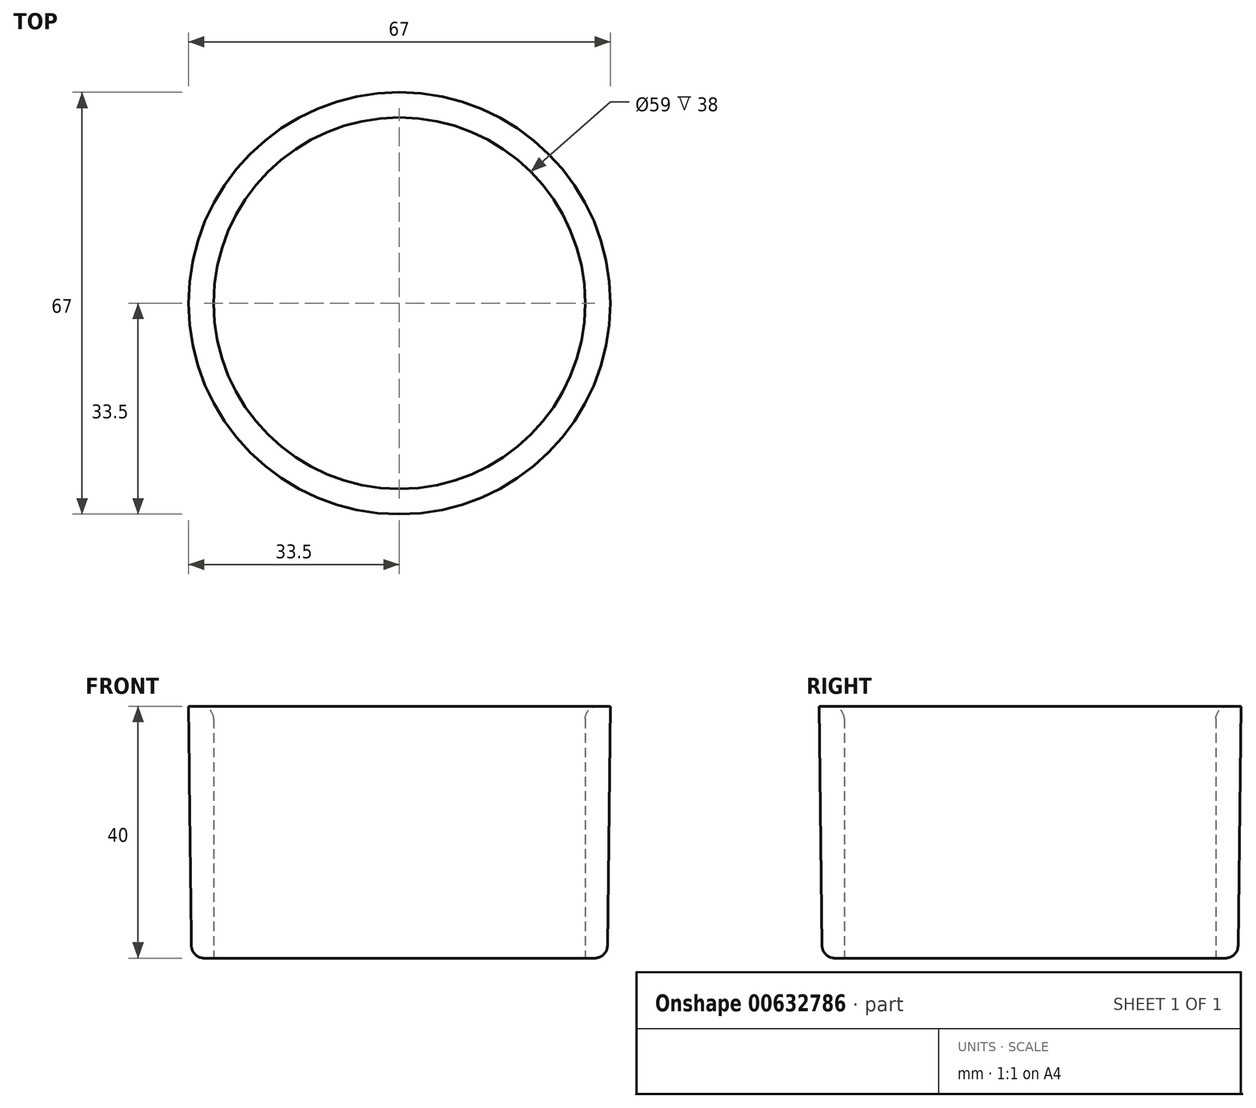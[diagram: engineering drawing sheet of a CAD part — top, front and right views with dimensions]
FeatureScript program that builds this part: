
annotation { "Feature Type Name" : "Feature", "Feature Type Description" : "" }
export const myFeature = defineFeature(function(context is Context, id is Id, definition is map)
    precondition{}
    {
        {
            var Q0;
            Q0=qCreatedBy(makeId("Front.planeOp"),FACE);
            var sketch = newSketch(context, id + "F0", { "sketchPlane" : qUnion([Q0])});
            skLineSegment(sketch, "E0", {"start": v(29.5, 0) * mm, "end": v(29.5, 40) * mm});
            skLineSegment(sketch, "E1", {"start": v(29.5, 40) * mm, "end": v(33.5, 40) * mm});
            skLineSegment(sketch, "E2", {"start": v(29.5, 0) * mm, "end": v(33.5, 0) * mm});
            skLineSegment(sketch, "E3", {"start": v(33.5, 40) * mm, "end": v(33.5, 0) * mm});
            skSolve(sketch);
        }
        {
            var Q0;
            Q0=qCreatedBy(makeId("Front.planeOp"),FACE);
            var sketch = newSketch(context, id + "F1", { "sketchPlane" : qUnion([Q0])});
            skLineSegment(sketch, "E4", {"start": v(0, 0) * mm, "end": v(0, 29.93) * mm});
            skSolve(sketch);
        }
        {
            var Q0;
            Q0=makeQuery(id+"F0.imprint","IMPRINT",FACE,{"disambiguationData":[TD([[makeQuery(id+"F0.imprint","IMPRINT",EDGE,{"derivedFrom":sQuery(id+"F0.wireOp",EDGE,"E0")}),-1.0]])]});
            var Q1;
            Q1=sQuery(id+"F1.wireOp",EDGE,"E4");
            revolve(context, id + "F2", {"entities" : qUnion([Q0]), "axis" : qUnion([Q1]), "revolveType" : RevolveType.FULL});
        }
        {
            var Q0;
            Q0=makeQuery(id+"F2.opRevolve","SWEPT_EDGE",EDGE,{"disambiguationData":[OSD([sQuery(id+"F0.wireOp",EDGE,"E2"),sQuery(id+"F0.wireOp",EDGE,"E3")])]});
            chamfer(context, id + "F3", {"entities" : qUnion([Q0]), "chamferType" : ChamferType.TWO_OFFSETS, "width1" : .5 * mm, "oppositeDirection" : false, "width2" : 40 * mm, "tangentPropagation" : true});
        }
        {
            var Q0;
            Q0=makeQuery(id+"F2.opRevolve","SWEPT_EDGE",EDGE,{"disambiguationData":[OSD([sQuery(id+"F0.wireOp",EDGE,"E0"),sQuery(id+"F0.wireOp",EDGE,"E1")])]});
            var Q1;
            {var subQ0=sQuery(id+"F0.wireOp",EDGE,"E2");Q1=makeQuery(id+"F3.opChamfer","BLEND_EDGE",EDGE,{"blendedFrom":[makeQuery(id+"F2.opRevolve","SWEPT_EDGE",EDGE,{"disambiguationData":[OSD([subQ0,sQuery(id+"F0.wireOp",EDGE,"E3")])]}),makeQuery(id+"F2.opRevolve","SWEPT_FACE",FACE,{"disambiguationData":[OSD([subQ0])]})],"blendedInto":[makeQuery(id+"F2.opRevolve","SWEPT_FACE",FACE,{"disambiguationData":[OSD([subQ0])]})]});}
            fillet(context, id + "F4", {"entities" : qUnion([Q0, Q1]), "radius" : 2 * mm, "tangentPropagation" : true, "allowEdgeOverflow" : false});
        }
    });
